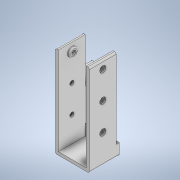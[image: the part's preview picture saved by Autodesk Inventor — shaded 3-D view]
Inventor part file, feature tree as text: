
AUTODESK INVENTOR PART (.ipt)
format: ipt  version: 2020 (Build 240168000, 168)  size: 285,184 bytes
history: native  units: in
note: dims shown in document units (in); Inventor stores cm internally (conversion verified against a paired STEP export)
features: extrude x12, sketch x12, fillet x3, mirror x2, pattern_linear x1
ambient origin geometry x8: Origin, YZ Plane, XZ Plane, XY Plane, X Axis, Y Axis, Z Axis, Center Point
bodies: Solid1 (feature_tree)
feature tree (30):
  extrude  "Extrusion1"  Depth=1.0in
  extrude  "Extrusion2"  Depth=0.1181in
  extrude  "Extrusion3"  Depth=3.2972in TaperAngle=0.0deg
  extrude  "Extrusion4"  Depth=0.1181in TaperAngle=0.0deg
  extrude  "Extrusion5"  Depth=0.0591in TaperAngle=0.0deg
  fillet  "Fillet1"  Radius=0.3346in
  pattern_linear  "Rectangular Pattern1"  Count1=3 Spacing1=-1.0236in
  mirror  "Mirror2"
  extrude  "Extrusion6"  Depth=1.2756in
  extrude  "Extrusion7"  Depth=0.6811in
  extrude  "Extrusion8"  Depth=0.2362in
  extrude  "Extrusion9"  Depth=0.0787in
  fillet  "Fillet2"  Radius=0.0787in
  extrude  "Extrusion11"  Depth=0.1181in TaperAngle=0.0deg
  extrude  "Extrusion14"  Depth=0.6496in
  mirror  "Mirror4"
  fillet  "Fillet5"  Radius=0.1181in
  extrude  "Extrusion15"  Depth=1.0in TaperAngle=0.0deg
  sketch  "Sketch1"  dims[d0=1.2756in d1=1.0in]
  sketch  "Sketch2"  dims[d2=0.1181in d3=0.0in d4=0.1181in]
  sketch  "Sketch3"  dims[d5=0.1181in d6=3.2972in d7=0.0in]
  sketch  "Sketch4"  dims[d8=0.1575in d9=0.1181in d10=0.0in]
  sketch  "Sketch5"  dims[d11=0.2362in d12=0.0591in d13=0.0in d14=0.3346in]
  sketch  "Sketch6"  dims[d15=0.0787in d16=0.0in]
  sketch  "Sketch7"  dims[d17=0.0472in d18=1.1811in d20=-1.0236in]
  sketch  "Sketch8"  dims[d21=0.1181in d22=1.2756in]
  sketch  "Sketch9"  dims[d23=0.6811in d24=0.0in d25=0.1575in]
  sketch  "Sketch11"  dims[d26=0.1181in d27=0.0in d28=0.2362in]
  sketch  "Sketch14"  dims[d29=0.0591in d30=0.0in d31=0.3346in d32=0.0787in d33=0.0in]
  sketch  "Sketch15"  dims[d34=0.0591in d38=0.1181in d39=0.0in d48=0.6496in d49=0.1181in d50=1.0in d51=0.0in d53=0.0591in d54=1.5748in d55=0.0in]
